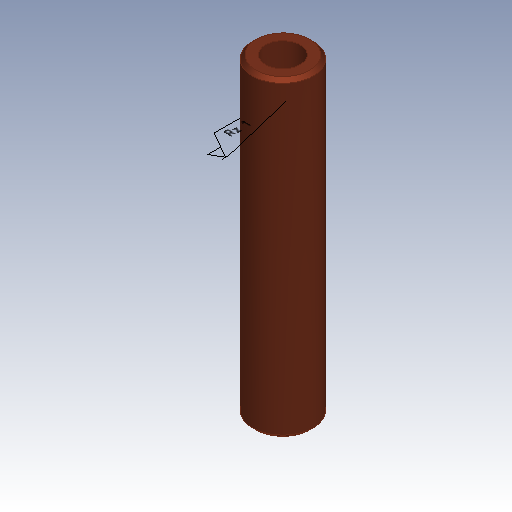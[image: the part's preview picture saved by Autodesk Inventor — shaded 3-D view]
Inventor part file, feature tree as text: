
AUTODESK INVENTOR PART (.ipt)
format: ipt  version: 2023.3 (Build 273359000, 359)  size: 143,872 bytes
history: native  units: in
note: dims shown in document units (in); Inventor stores cm internally (conversion verified against a paired STEP export)
features: other x2, extrude x1, chamfer x1, sketch x1
ambient origin geometry x8: Origin, YZ Plane, XZ Plane, XY Plane, X Axis, Y Axis, Z Axis, Center Point
bodies: Body1 (feature_tree)
feature tree (5):
  other  "Anmerkungen"
  extrude  "Extrusion3"  Depth=0.7087in
  chamfer  "Fase1"  Distance=0.7087in
  sketch  "Skizze3"  dims[d4=0.0787in d5=0.0295in d6=0.7087in d7=0.0in d8=0.0079in d9=0.0787in d10=45.0deg d11=0.3689in d12=0.1044in]
  other  "Oberflächenbeschaffenheit 1"
